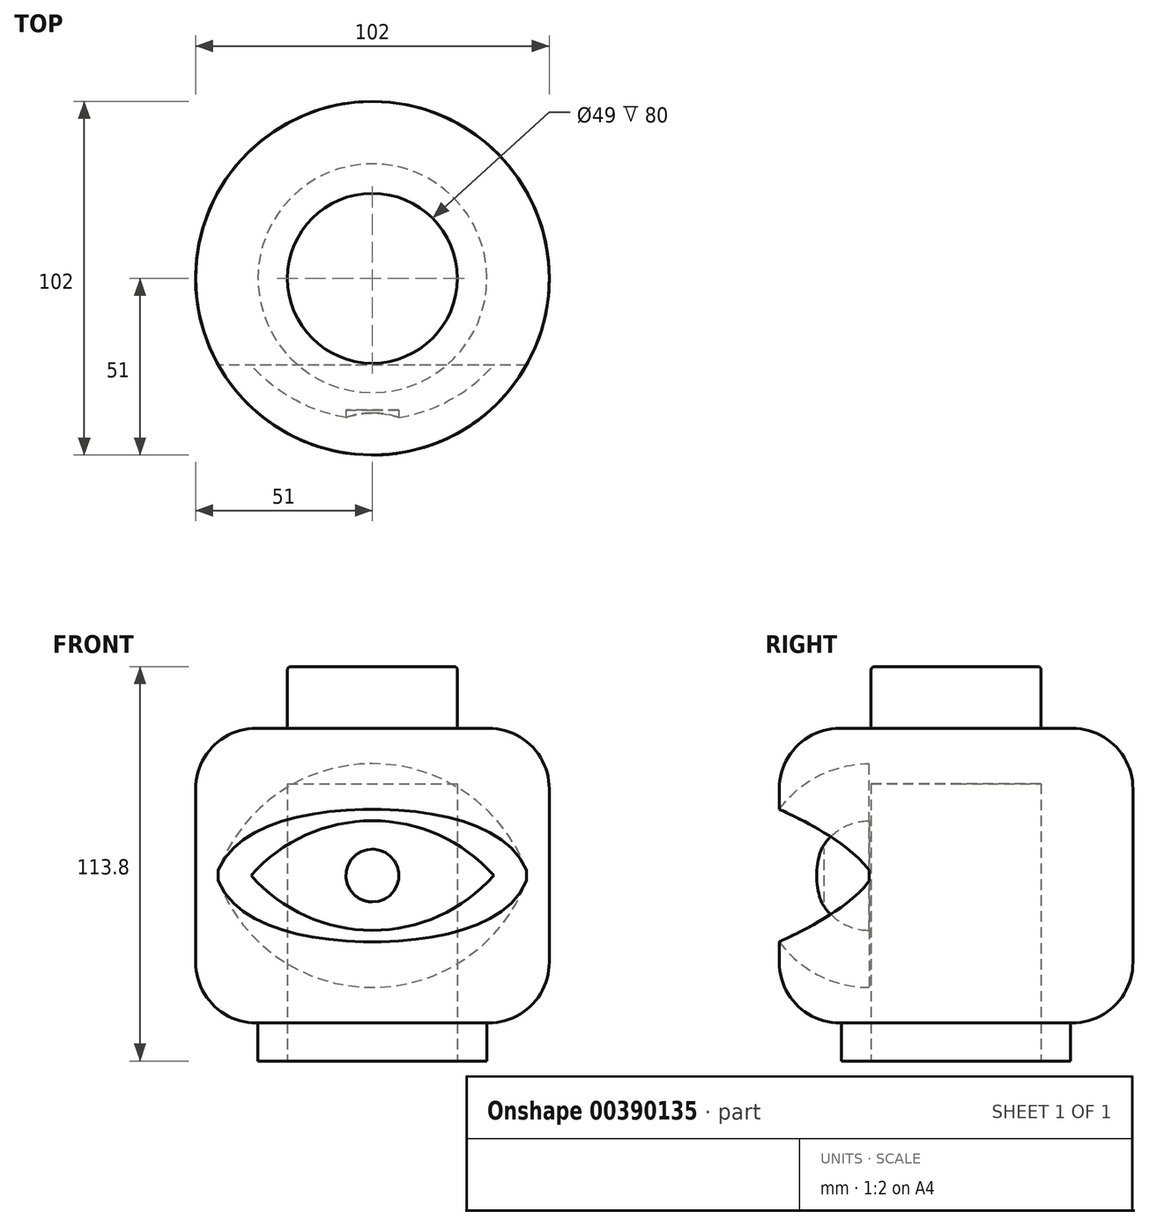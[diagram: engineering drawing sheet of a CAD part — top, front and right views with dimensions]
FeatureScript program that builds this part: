
annotation { "Feature Type Name" : "Feature", "Feature Type Description" : "" }
export const myFeature = defineFeature(function(context is Context, id is Id, definition is map)
    precondition{}
    {
        {
            var Q0;
            Q0=qCreatedBy(makeId("Top.planeOp"),FACE);
            var sketch = newSketch(context, id + "F0", { "sketchPlane" : qUnion([Q0])});
            skCircle(sketch, "E0", {"center": v(0, 0) * mm, "radius": 51 * mm});
            skSolve(sketch);
        }
        {
            var Q0;
            Q0=makeQuery(id+"F0.imprint","IMPRINT",FACE,{"disambiguationData":[TD([[makeQuery(id+"F0.imprint","IMPRINT",EDGE,{"derivedFrom":sQuery(id+"F0.wireOp",EDGE,"E0")}),1.0]])]});
            extrude(context, id + "F1", {"entities" : qUnion([Q0]), "depth" : 42.5 * mm});
        }
        {
            var Q0;
            Q0=makeQuery(id+"F1.opExtrude","CAP_FACE",FACE,{"disambiguationData":[OSD([sQuery(id+"F0.wireOp",EDGE,"E0")])],"isStart":false});
            fillet(context, id + "F2", {"entities" : qUnion([Q0]), "radius" : 17.5 * mm, "tangentPropagation" : true, "allowEdgeOverflow" : false});
        }
        {
            var Q0;
            Q0=makeQuery(id+"F1.opExtrude","CAP_FACE",FACE,{"disambiguationData":[OSD([sQuery(id+"F0.wireOp",EDGE,"E0")])],"isStart":false});
            var sketch = newSketch(context, id + "F3", { "sketchPlane" : qUnion([Q0])});
            skCircle(sketch, "E1", {"center": v(0, 0) * mm, "radius": 24.5 * mm});
            skSolve(sketch);
        }
        {
            var Q0;
            Q0=makeQuery(id+"F3.imprint","IMPRINT",FACE,{"disambiguationData":[TD([[makeQuery(id+"F3.imprint","IMPRINT",EDGE,{"derivedFrom":sQuery(id+"F3.wireOp",EDGE,"E1")}),1.0]])]});
            extrude(context, id + "F4", {"entities" : qUnion([Q0]), "operationType" : NewBodyOperationType.ADD, "depth" : 17.8 * mm});
        }
        {
            var Q0;
            Q0=makeQuery(id+"F4.opExtrude","CAP_EDGE",EDGE,{"disambiguationData":[OSD([sQuery(id+"F3.wireOp",EDGE,"E1")])],"isStart":false});
            fillet(context, id + "F5", {"entities" : qUnion([Q0]), "radius" : 1 * mm, "tangentPropagation" : true, "allowEdgeOverflow" : false});
        }
        {
            var Q0;
            Q0=makeQuery(id+"F1.opExtrude","CAP_FACE",FACE,{"disambiguationData":[OSD([sQuery(id+"F0.wireOp",EDGE,"E0")])],"isStart":true});
            extrude(context, id + "F6", {"entities" : qUnion([Q0]), "operationType" : NewBodyOperationType.ADD, "depth" : 42.5 * mm});
        }
        {
            var Q0;
            Q0=makeQuery(id+"F6.opExtrude","CAP_FACE",FACE,{"disambiguationData":[OSD([sQuery(id+"F0.wireOp",EDGE,"E0")])],"isStart":false});
            var sketch = newSketch(context, id + "F7", { "sketchPlane" : qUnion([Q0])});
            skCircle(sketch, "E2", {"center": v(0, 0) * mm, "radius": 33 * mm});
            skSolve(sketch);
        }
        {
            var Q0;
            Q0=makeQuery(id+"F7.imprint","IMPRINT",FACE,{"disambiguationData":[TD([[makeQuery(id+"F7.imprint","IMPRINT",EDGE,{"derivedFrom":sQuery(id+"F7.wireOp",EDGE,"E2")}),1.0]])]});
            extrude(context, id + "F8", {"entities" : qUnion([Q0]), "operationType" : NewBodyOperationType.ADD, "depth" : 11 * mm, "offsetDistance" : 25 * mm});
        }
        {
            var Q0;
            Q0=makeQuery(id+"F8.opExtrude","CAP_FACE",FACE,{"disambiguationData":[OSD([sQuery(id+"FBTceW7lFiRSeCQ_1.wireOp",EDGE,"hVqF75ZI-vp8t-1vhN-kkoJ-N5fIvlzN1McN"),sQuery(id+"F7.wireOp",EDGE,"E2")])],"isStart":false});
            var sketch = newSketch(context, id + "F9", { "sketchPlane" : qUnion([Q0])});
            skCircle(sketch, "E3", {"center": v(0, 0) * mm, "radius": 24.5 * mm});
            skSolve(sketch);
        }
        {
            var Q0;
            Q0=makeQuery(id+"F9.imprint","IMPRINT",FACE,{"disambiguationData":[TD([[makeQuery(id+"F9.imprint","IMPRINT",EDGE,{"derivedFrom":sQuery(id+"F9.wireOp",EDGE,"E3")}),1.0]])]});
            extrude(context, id + "F10", {"entities" : qUnion([Q0]), "operationType" : NewBodyOperationType.REMOVE, "oppositeDirection" : true, "depth" : 80 * mm, "offsetDistance" : 25 * mm});
        }
        {
            var Q0;
            Q0=makeQuery(id+"F6.opExtrude","CAP_EDGE",EDGE,{"disambiguationData":[OSD([sQuery(id+"F0.wireOp",EDGE,"E0")])],"isStart":false});
            fillet(context, id + "F11", {"entities" : qUnion([Q0]), "radius" : 17.5 * mm, "tangentPropagation" : true, "allowEdgeOverflow" : false});
        }
        {
            var Q0;
            Q0=qCreatedBy(makeId("Front.planeOp"),FACE);
            cPlane(context, id + "F12", {"entities" : qUnion([Q0]), "cplaneType" : CPlaneType.OFFSET, "offset" : 25 * mm, "width" : 150 * mm, "height" : 150 * mm});
        }
        {
            var Q0;
            Q0=qCreatedBy(id+"F12.planeOp",FACE);
            var sketch = newSketch(context, id + "F13", { "sketchPlane" : qUnion([Q0])});
            skArc(sketch, "E4", {"start": v(35, 0) * mm, "mid": v(0, 15.49) * mm, "end": v(-35, 0) * mm});
            skLineSegment(sketch, "E5", {"start": v(-35, 0) * mm, "end": v(35, 0) * mm});
            skSolve(sketch);
        }
        {
            var Q0;
            Q0=makeQuery(id+"F13.imprint","IMPRINT",FACE,{"disambiguationData":[TD([[makeQuery(id+"F13.imprint","IMPRINT",EDGE,{"derivedFrom":sQuery(id+"F13.wireOp",EDGE,"E4")}),1.0]])]});
            var Q1;
            Q1=sQuery(id+"F13.wireOp",EDGE,"E5");
            revolve(context, id + "F14", {"surfaceOperationType" : NewSurfaceOperationType.NEW, "entities" : qUnion([Q0]), "axis" : qUnion([Q1]), "revolveType" : RevolveType.FULL});
        }
        {
            var Q0;
            Q0=qCreatedBy(makeId("Front.planeOp"),FACE);
            cPlane(context, id + "F15", {"entities" : qUnion([Q0]), "cplaneType" : CPlaneType.OFFSET, "offset" : 25 * mm, "width" : 150 * mm, "height" : 150 * mm});
        }
        {
            var Q0;
            Q0=qCreatedBy(id+"F15.planeOp",FACE);
            var sketch = newSketch(context, id + "F16", { "sketchPlane" : qUnion([Q0])});
            skArc(sketch, "E6", {"start": v(45, 0) * mm, "mid": v(0, 32.27) * mm, "end": v(-45, 0) * mm});
            skLineSegment(sketch, "E7", {"start": v(-45, 0) * mm, "end": v(45, 0) * mm});
            skArc(sketch, "E8", {"start": v(35, 0) * mm, "mid": v(0, 15.8) * mm, "end": v(-35, 0) * mm});
            skSolve(sketch);
        }
        {
            var Q0;
            {var subQ0=sQuery(id+"F16.wireOp",EDGE,"E6");Q0=makeQuery(id+"F16.imprint","IMPRINT",FACE,{"disambiguationData":[TD([[makeQuery(id+"F16.imprint","IMPRINT",EDGE,{"derivedFrom":subQ0}),1.0]])]});}
            var Q1;
            Q1=sQuery(id+"F16.wireOp",EDGE,"E7");
            revolve(context, id + "F17", {"operationType" : NewBodyOperationType.REMOVE, "surfaceOperationType" : NewSurfaceOperationType.NEW, "entities" : qUnion([Q0]), "axis" : qUnion([Q1]), "revolveType" : RevolveType.ONE_DIRECTION, "angle" : 180 * degree});
        }
        {
            var Q0;
            Q0=qCreatedBy(makeId("Front.planeOp"),FACE);
            cPlane(context, id + "F18", {"entities" : qUnion([Q0]), "cplaneType" : CPlaneType.OFFSET, "offset" : 45 * mm, "width" : 150 * mm, "height" : 150 * mm});
        }
        {
            var Q0;
            Q0=qCreatedBy(id+"F18.planeOp",FACE);
            var sketch = newSketch(context, id + "F19", { "sketchPlane" : qUnion([Q0])});
            skCircle(sketch, "E9", {"center": v(0, 0) * mm, "radius": 7.6 * mm});
            skSolve(sketch);
        }
        {
            var Q0;
            Q0=makeQuery(id+"F19.imprint","IMPRINT",FACE,{"disambiguationData":[TD([[makeQuery(id+"F19.imprint","IMPRINT",EDGE,{"derivedFrom":sQuery(id+"F19.wireOp",EDGE,"E9")}),1.0]])]});
            extrude(context, id + "F20", {"entities" : qUnion([Q0]), "operationType" : NewBodyOperationType.REMOVE, "oppositeDirection" : true, "depth" : 7 * mm, "offsetDistance" : 25 * mm});
        }
        {
            var Q0;
            Q0=makeQuery(id+"F8.opExtrude","CAP_FACE",FACE,{"disambiguationData":[OSD([sQuery(id+"F7.wireOp",EDGE,"E2")])],"isStart":false});
            var sketch = newSketch(context, id + "F21", { "sketchPlane" : qUnion([Q0])});
            skCircle(sketch, "E10", {"center": v(0, 0) * mm, "radius": 24.25 * mm});
            skSolve(sketch);
        }
        {
            var Q0;
            Q0=makeQuery(id+"F21.imprint","IMPRINT",FACE,{"disambiguationData":[TD([[makeQuery(id+"F21.imprint","IMPRINT",EDGE,{"derivedFrom":sQuery(id+"F21.wireOp",EDGE,"E10")}),1.0]])]});
            extrude(context, id + "F22", {"entities" : qUnion([Q0]), "operationType" : NewBodyOperationType.REMOVE, "oppositeDirection" : true, "depth" : 80 * mm, "offsetDistance" : 25 * mm});
        }
        {
            var Q0;
            Q0=makeQuery(id+"F14.opRevolve","SWEPT_BODY",BODY,{"disambiguationData":[OSD([sQuery(id+"F13.wireOp",EDGE,"E4"),sQuery(id+"F13.wireOp",EDGE,"E5")])]});
            deleteBodies(context, id + "F23", {"entities" : qUnion([Q0])});
        }
    });
